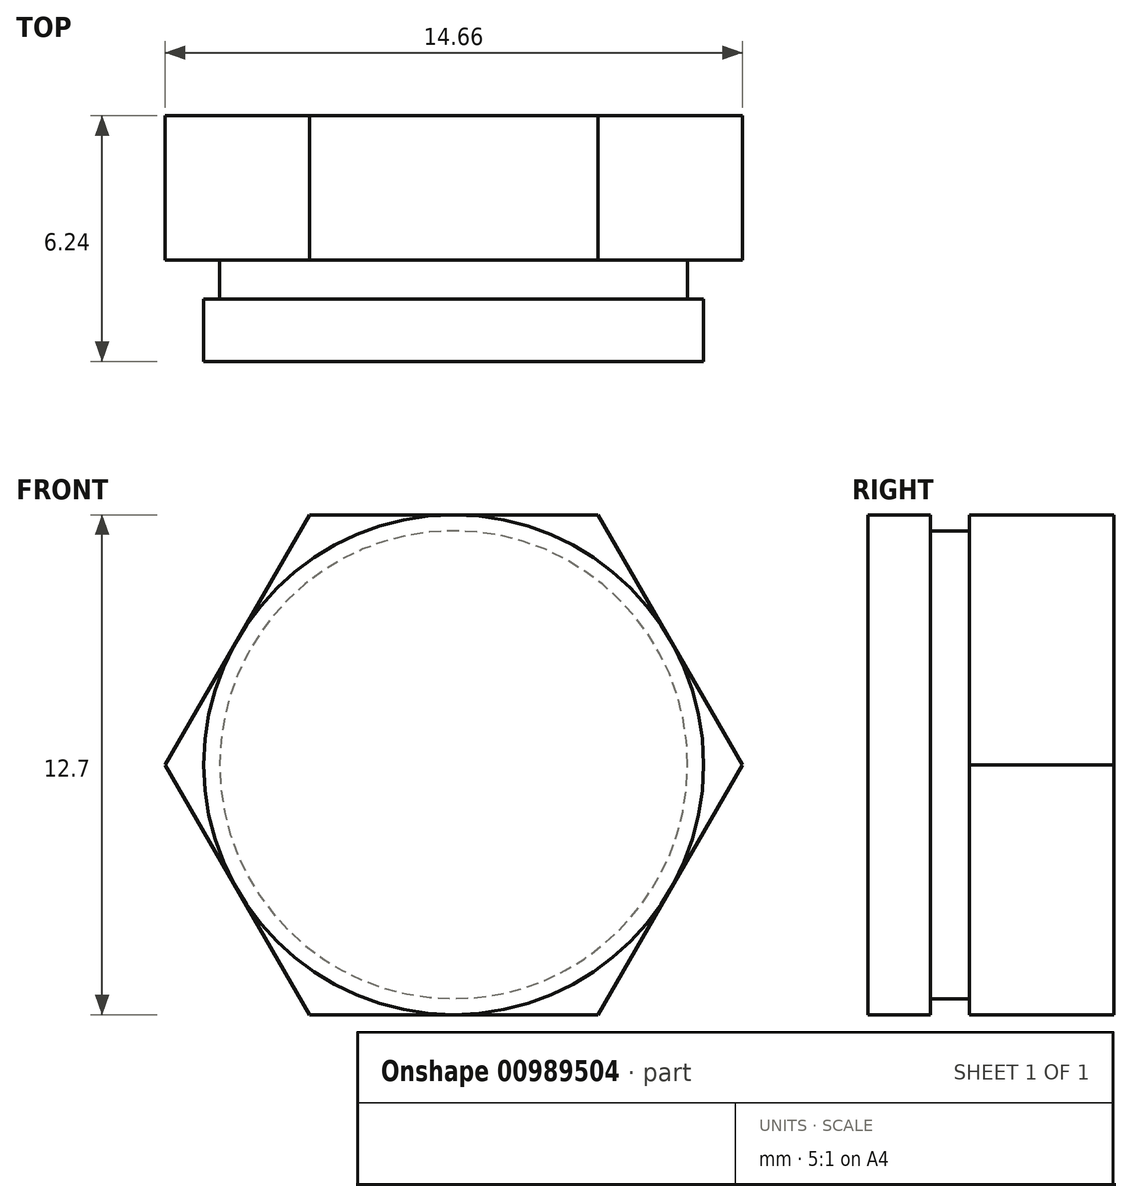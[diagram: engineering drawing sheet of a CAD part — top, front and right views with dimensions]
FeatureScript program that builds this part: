
annotation { "Feature Type Name" : "Feature", "Feature Type Description" : "" }
export const myFeature = defineFeature(function(context is Context, id is Id, definition is map)
    precondition{}
    {
        {
            var Q0;
            Q0=qCreatedBy(makeId("Front.planeOp"),FACE);
            var sketch = newSketch(context, id + "F0", { "sketchPlane" : qUnion([Q0])});
            skCircle(sketch, "E0.cCircle", {"center": v(0, 0) * mm, "radius": 6.35 * mm, "construction": true});
            skLineSegment(sketch, "E0.0", {"start": v(-3.67, 6.35) * mm, "end": v(3.67, 6.35) * mm});
            skLineSegment(sketch, "E0.1", {"start": v(3.67, 6.35) * mm, "end": v(7.33, 0) * mm});
            skLineSegment(sketch, "E0.2", {"start": v(7.33, 0) * mm, "end": v(3.67, -6.35) * mm});
            skLineSegment(sketch, "E0.3", {"start": v(3.67, -6.35) * mm, "end": v(-3.67, -6.35) * mm});
            skLineSegment(sketch, "E0.4", {"start": v(-3.67, -6.35) * mm, "end": v(-7.33, 0) * mm});
            skLineSegment(sketch, "E0.5", {"start": v(-7.33, 0) * mm, "end": v(-3.67, 6.35) * mm});
            skPoint(sketch, "E0.0.midPoint", {"position": v(0, 6.35) * mm});
            skSolve(sketch);
        }
        {
            var Q0;
            Q0=qSketchRegion(id+"F0",true);
            extrude(context, id + "F1", {"entities" : qUnion([Q0]), "depth" : ((4.03 - 0.36) / 2) * mm, "offsetDistance" : 25.4 * mm, "hasSecondDirection" : true, "secondDirectionOppositeDirection" : true, "secondDirectionDepth" : ((4.03 - 0.36) / 2) * mm});
        }
        {
            var Q0;
            Q0=makeQuery(id+"F1.opExtrude","CAP_FACE",FACE,{"disambiguationData":[OSD([sQuery(id+"F0.wireOp",EDGE,"E0.0"),sQuery(id+"F0.wireOp",EDGE,"E0.1"),sQuery(id+"F0.wireOp",EDGE,"E0.2"),sQuery(id+"F0.wireOp",EDGE,"E0.3"),sQuery(id+"F0.wireOp",EDGE,"E0.4"),sQuery(id+"F0.wireOp",EDGE,"E0.5")])],"isStart":false});
            var sketch = newSketch(context, id + "F2", { "sketchPlane" : qUnion([Q0])});
            skCircle(sketch, "E1", {"center": v(0, 0) * mm, "radius": 5.94 * mm});
            skSolve(sketch);
        }
        {
            var Q0;
            Q0=qSketchRegion(id+"F2",true);
            extrude(context, id + "F3", {"entities" : qUnion([Q0]), "operationType" : NewBodyOperationType.ADD, "depth" : 1 * mm, "offsetDistance" : 25.4 * mm});
        }
        {
            var Q0;
            Q0=makeQuery(id+"F3.opExtrude","CAP_FACE",FACE,{"disambiguationData":[OSD([sQuery(id+"F2.wireOp",EDGE,"E1")])],"isStart":false});
            var sketch = newSketch(context, id + "F4", { "sketchPlane" : qUnion([Q0])});
            skCircle(sketch, "E2", {"center": v(0, 0) * mm, "radius": 6.35 * mm});
            skSolve(sketch);
        }
        {
            var Q0;
            Q0=qSketchRegion(id+"F4",true);
            extrude(context, id + "F5", {"entities" : qUnion([Q0]), "operationType" : NewBodyOperationType.ADD, "depth" : 1.59 * mm, "offsetDistance" : 25.4 * mm});
        }
    });
